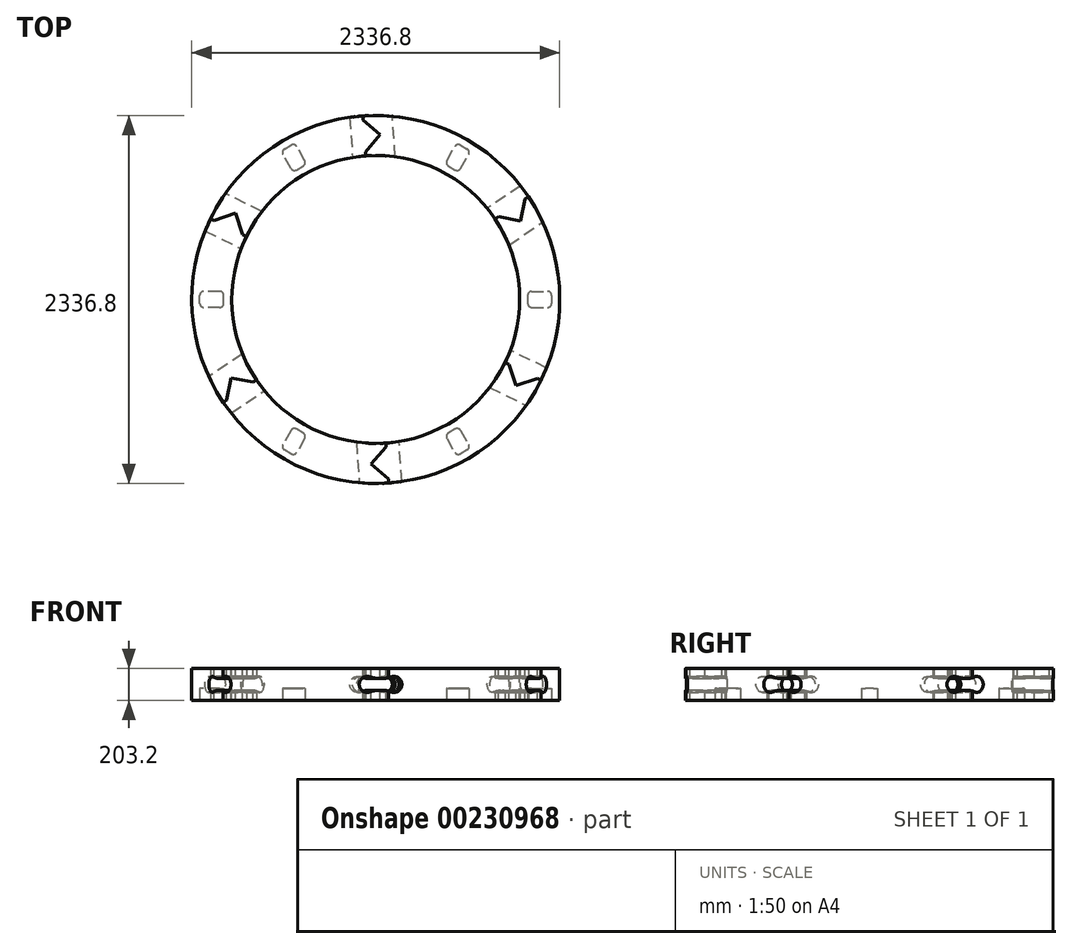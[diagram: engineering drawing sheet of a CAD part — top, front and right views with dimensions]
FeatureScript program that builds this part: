
annotation { "Feature Type Name" : "Feature", "Feature Type Description" : "" }
export const myFeature = defineFeature(function(context is Context, id is Id, definition is map)
    precondition{}
    {
        {
            var Q0;
            Q0=qCreatedBy(makeId("Front.planeOp"),FACE);
            var sketch = newSketch(context, id + "F0", { "sketchPlane" : qUnion([Q0])});
            skLineSegment(sketch, "E0.bottom", {"start": v(-1168.4, 101.6) * mm, "end": v(-914.4, 101.6) * mm});
            skLineSegment(sketch, "E0.top", {"start": v(-1168.4, -101.6) * mm, "end": v(-914.4, -101.6) * mm});
            skLineSegment(sketch, "E0.left", {"start": v(-1168.4, 101.6) * mm, "end": v(-1168.4, -101.6) * mm});
            skLineSegment(sketch, "E0.right", {"start": v(-914.4, 101.6) * mm, "end": v(-914.4, -101.6) * mm});
            skPoint(sketch, "E0.middle", {"position": v(-1041.4, 0) * mm});
            skLineSegment(sketch, "E1", {"start": v(0, 122.44) * mm, "end": v(0, -122.44) * mm, "construction": true});
            skSolve(sketch);
        }
        {
            var Q0;
            Q0=makeQuery(id+"F0.imprint","IMPRINT",FACE,{"disambiguationData":[TD([[makeQuery(id+"F0.imprint","IMPRINT",EDGE,{"derivedFrom":sQuery(id+"F0.wireOp",EDGE,"E0.bottom")}),-1.0]])]});
            var Q1;
            Q1=sQuery(id+"F0.wireOp",EDGE,"E1");
            revolve(context, id + "F1", {"entities" : qUnion([Q0]), "axis" : qUnion([Q1]), "revolveType" : RevolveType.TWO_DIRECTIONS, "angle" : 26 * degree, "angleBack" : 326 * degree});
        }
        {
            var Q0;
            Q0=makeQuery(id+"F1.opRevolve","SWEPT_FACE",FACE,{"disambiguationData":[OSD([sQuery(id+"F0.wireOp",EDGE,"E0.bottom")])]});
            var sketch = newSketch(context, id + "F2", { "sketchPlane" : qUnion([Q0])});
            skLineSegment(sketch, "E2", {"start": v(-1027.32, 501.06) * mm, "end": v(-891.47, 547.84) * mm});
            skLineSegment(sketch, "E3", {"start": v(-891.47, 547.84) * mm, "end": v(-844.69, 411.98) * mm});
            skSolve(sketch);
        }
        {
            var Q0;
            Q0=makeQuery(id+"F2.imprint","IMPRINT",FACE,{"disambiguationData":[TD([[makeQuery(id+"F2.imprint","IMPRINT",EDGE,{"derivedFrom":sQuery(id+"F2.wireOp",EDGE,"E2")}),-1.0]])]});
            var Q1;
            Q1=makeQuery(id+"F1.opRevolve","SWEPT_FACE",FACE,{"disambiguationData":[OSD([sQuery(id+"F0.wireOp",EDGE,"E0.top")])]});
            extrude(context, id + "F3", {"entities" : qUnion([Q0]), "operationType" : NewBodyOperationType.ADD, "endBound" : BoundingType.UP_TO_SURFACE, "oppositeDirection" : true, "endBoundEntityFace" : qUnion([Q1]), "depth" : 25.4 * mm});
        }
        {
            var Q0;
            {var subQ0=sQuery(id+"F0.wireOp",EDGE,"E0.bottom");Q0=makeQuery(id+"F3.boolean.opBoolean","MERGE",FACE,{"derivedFrom":[makeQuery(id+"F1.opRevolve","SWEPT_FACE",FACE,{"disambiguationData":[OSD([subQ0])]}),makeQuery(id+"F3.opExtrude","CAP_FACE",FACE,{"disambiguationData":[OSD([subQ0,sQuery(id+"F2.wireOp",EDGE,"E2"),sQuery(id+"F2.wireOp",EDGE,"E3")])],"isStart":true})]});}
            var sketch = newSketch(context, id + "F4", { "sketchPlane" : qUnion([Q0])});
            skLineSegment(sketch, "E4", {"start": v(-947.59, -639.16) * mm, "end": v(-920.17, -498.11) * mm});
            skLineSegment(sketch, "E5", {"start": v(-920.17, -498.11) * mm, "end": v(-779.13, -525.53) * mm});
            skSolve(sketch);
        }
        {
            var Q0;
            Q0=qSketchRegion(id+"F4",true);
            var Q1;
            Q1=makeQuery(id+"F4.imprint","IMPRINT",FACE,{"disambiguationData":[TD([[makeQuery(id+"F4.imprint","IMPRINT",EDGE,{"derivedFrom":sQuery(id+"F4.wireOp",EDGE,"E4")}),-1.0]])]});
            var Q2;
            {var subQ0=sQuery(id+"F0.wireOp",EDGE,"E0.top");Q2=makeQuery(id+"F3.boolean.opBoolean","MERGE",FACE,{"derivedFrom":[makeQuery(id+"F1.opRevolve","SWEPT_FACE",FACE,{"disambiguationData":[OSD([subQ0])]}),makeQuery(id+"F3.opExtrude","CAP_FACE",FACE,{"disambiguationData":[OSD([subQ0])],"isStart":false})]});}
            extrude(context, id + "F5", {"entities" : qUnion([Q0, Q1]), "operationType" : NewBodyOperationType.REMOVE, "endBound" : BoundingType.UP_TO_SURFACE, "oppositeDirection" : true, "endBoundEntityFace" : qUnion([Q2]), "depth" : 25.4 * mm});
        }
        {
            var Q0;
            Q0=makeQuery(id+"F3.opExtrude","SWEPT_EDGE",EDGE,{"disambiguationData":[OSD([sQuery(id+"F2.wireOp",EDGE,"E2"),sQuery(id+"F2.wireOp",EDGE,"E3")])]});
            var Q1;
            Q1=makeQuery(id+"F3.opExtrude","SWEPT_FACE",FACE,{"disambiguationData":[OSD([sQuery(id+"F2.wireOp",EDGE,"E2")])]});
            cPlane(context, id + "F6", {"entities" : qUnion([Q0, Q1]), "cplaneType" : CPlaneType.LINE_ANGLE, "offset" : 25.4 * mm, "angle" : 45 * degree, "width" : 152.4 * mm, "height" : 152.4 * mm});
        }
        {
            var Q0;
            Q0=makeQuery(id+"F5.boolean.opBoolean","COPY",EDGE,{"derivedFrom":makeQuery(id+"F5.opExtrude","SWEPT_EDGE",EDGE,{"disambiguationData":[OSD([sQuery(id+"F4.wireOp",EDGE,"E4"),sQuery(id+"F4.wireOp",EDGE,"E5")])]})});
            var Q1;
            Q1=makeQuery(id+"F5.boolean.opBoolean","COPY",FACE,{"derivedFrom":makeQuery(id+"F5.opExtrude","SWEPT_FACE",FACE,{"disambiguationData":[OSD([sQuery(id+"F4.wireOp",EDGE,"E4")])]})});
            cPlane(context, id + "F7", {"entities" : qUnion([Q0, Q1]), "cplaneType" : CPlaneType.LINE_ANGLE, "offset" : 25.4 * mm, "angle" : 45 * degree, "width" : 152.4 * mm, "height" : 152.4 * mm});
        }
        {
            var Q0;
            Q0=qCreatedBy(id+"F6.planeOp",FACE);
            var sketch = newSketch(context, id + "F8", { "sketchPlane" : qUnion([Q0])});
            skArc(sketch, "E6", {"start": v(-15.92, 47.62) * mm, "mid": v(-84.4, 0) * mm, "end": v(-15.92, -47.63) * mm});
            skArc(sketch, "E7", {"start": v(117.52, -47.63) * mm, "mid": v(186, 0) * mm, "end": v(117.52, 47.62) * mm});
            skLineSegment(sketch, "E8", {"start": v(37.1, 38.1) * mm, "end": v(64.5, 38.1) * mm});
            skLineSegment(sketch, "E9", {"start": v(37.1, -38.1) * mm, "end": v(64.5, -38.1) * mm});
            skPoint(sketch, "E10.visualSharp", {"position": v(0, 38.1) * mm});
            skArc(sketch, "E10.filletArc", {"start": v(-15.92, 47.63) * mm, "mid": v(10.17, 40.5) * mm, "end": v(37.1, 38.1) * mm});
            skPoint(sketch, "E11.visualSharp", {"position": v(101.6, 38.1) * mm});
            skArc(sketch, "E11.filletArc", {"start": v(64.5, 38.1) * mm, "mid": v(91.43, 40.5) * mm, "end": v(117.52, 47.63) * mm});
            skPoint(sketch, "E12.visualSharp", {"position": v(101.6, -38.1) * mm});
            skArc(sketch, "E12.filletArc", {"start": v(117.52, -47.63) * mm, "mid": v(91.43, -40.5) * mm, "end": v(64.5, -38.1) * mm});
            skPoint(sketch, "E13.visualSharp", {"position": v(0, -38.1) * mm});
            skArc(sketch, "E13.filletArc", {"start": v(37.1, -38.1) * mm, "mid": v(10.17, -40.5) * mm, "end": v(-15.92, -47.63) * mm});
            skSolve(sketch);
        }
        {
            var Q0;
            Q0=qSketchRegion(id+"F8",true);
            extrude(context, id + "F9", {"entities" : qUnion([Q0]), "operationType" : NewBodyOperationType.REMOVE, "endBound" : BoundingType.SYMMETRIC, "oppositeDirection" : true, "depth" : 508 * mm});
        }
        {
            var Q0;
            Q0=qCreatedBy(id+"F7.planeOp",FACE);
            var sketch = newSketch(context, id + "F10", { "sketchPlane" : qUnion([Q0])});
            skArc(sketch, "E14", {"start": v(-117.52, 47.63) * mm, "mid": v(-186, 0) * mm, "end": v(-117.52, -47.63) * mm});
            skArc(sketch, "E15", {"start": v(15.92, -47.63) * mm, "mid": v(84.4, 0) * mm, "end": v(15.92, 47.63) * mm});
            skLineSegment(sketch, "E16", {"start": v(-37.1, 38.1) * mm, "end": v(-64.5, 38.1) * mm});
            skLineSegment(sketch, "E17", {"start": v(-37.1, -38.1) * mm, "end": v(-64.5, -38.1) * mm});
            skPoint(sketch, "E18.visualSharp", {"position": v(0, 38.1) * mm});
            skArc(sketch, "E18.filletArc", {"start": v(-37.1, 38.1) * mm, "mid": v(-10.17, 40.5) * mm, "end": v(15.92, 47.63) * mm});
            skPoint(sketch, "E19.visualSharp", {"position": v(-101.6, 38.1) * mm});
            skArc(sketch, "E19.filletArc", {"start": v(-117.52, 47.62) * mm, "mid": v(-91.43, 40.5) * mm, "end": v(-64.5, 38.1) * mm});
            skPoint(sketch, "E20.visualSharp", {"position": v(-101.6, -38.1) * mm});
            skArc(sketch, "E20.filletArc", {"start": v(-64.5, -38.1) * mm, "mid": v(-91.43, -40.5) * mm, "end": v(-117.52, -47.62) * mm});
            skPoint(sketch, "E21.visualSharp", {"position": v(0, -38.1) * mm});
            skArc(sketch, "E21.filletArc", {"start": v(15.92, -47.63) * mm, "mid": v(-10.17, -40.5) * mm, "end": v(-37.1, -38.1) * mm});
            skSolve(sketch);
        }
        {
            var Q0;
            Q0=qSketchRegion(id+"F10",true);
            extrude(context, id + "F11", {"entities" : qUnion([Q0]), "operationType" : NewBodyOperationType.REMOVE, "endBound" : BoundingType.SYMMETRIC, "oppositeDirection" : true, "depth" : 508 * mm});
        }
        {
            var Q0;
            {var subQ0=sQuery(id+"F0.wireOp",EDGE,"E0.top");Q0=makeQuery(id+"F3.boolean.opBoolean","MERGE",FACE,{"derivedFrom":[makeQuery(id+"F1.opRevolve","SWEPT_FACE",FACE,{"disambiguationData":[OSD([subQ0])]}),makeQuery(id+"F3.opExtrude","CAP_FACE",FACE,{"disambiguationData":[OSD([subQ0])],"isStart":false})]});}
            var sketch = newSketch(context, id + "F12", { "sketchPlane" : qUnion([Q0])});
            skLineSegment(sketch, "E22.bottom", {"start": v(-990.6, 50.8) * mm, "end": v(-1092.2, 50.8) * mm});
            skLineSegment(sketch, "E22.top", {"start": v(-990.6, -50.8) * mm, "end": v(-1092.2, -50.8) * mm});
            skLineSegment(sketch, "E22.left", {"start": v(-965.2, 25.4) * mm, "end": v(-965.2, -25.4) * mm});
            skLineSegment(sketch, "E22.right", {"start": v(-1117.6, 25.4) * mm, "end": v(-1117.6, -25.4) * mm});
            skPoint(sketch, "E22.middle", {"position": v(-1041.4, 0) * mm});
            skPoint(sketch, "E23.visualSharp", {"position": v(-965.2, 50.8) * mm});
            skArc(sketch, "E23.filletArc", {"start": v(-965.2, 25.4) * mm, "mid": v(-972.64, 43.36) * mm, "end": v(-990.6, 50.8) * mm});
            skPoint(sketch, "E24.visualSharp", {"position": v(-965.2, -50.8) * mm});
            skArc(sketch, "E24.filletArc", {"start": v(-990.6, -50.8) * mm, "mid": v(-972.64, -43.36) * mm, "end": v(-965.2, -25.4) * mm});
            skPoint(sketch, "E25.visualSharp", {"position": v(-1117.6, -50.8) * mm});
            skArc(sketch, "E25.filletArc", {"start": v(-1117.6, -25.4) * mm, "mid": v(-1110.16, -43.36) * mm, "end": v(-1092.2, -50.8) * mm});
            skPoint(sketch, "E26.visualSharp", {"position": v(-1117.6, 50.8) * mm});
            skArc(sketch, "E26.filletArc", {"start": v(-1092.2, 50.8) * mm, "mid": v(-1110.16, 43.36) * mm, "end": v(-1117.6, 25.4) * mm});
            skSolve(sketch);
        }
        {
            var Q0;
            Q0=qSketchRegion(id+"F12",true);
            extrude(context, id + "F13", {"entities" : qUnion([Q0]), "operationType" : NewBodyOperationType.REMOVE, "oppositeDirection" : true, "depth" : 76.2 * mm});
        }
        {
            var Q0;
            Q0=makeQuery(id+"F1.opRevolve","SWEPT_BODY",BODY,{"disambiguationData":[OSD([sQuery(id+"F0.wireOp",EDGE,"E0.bottom"),sQuery(id+"F0.wireOp",EDGE,"E0.top"),sQuery(id+"F0.wireOp",EDGE,"E0.left"),sQuery(id+"F0.wireOp",EDGE,"E0.right")])]});
            var Q1;
            Q1=sQuery(id+"F0.wireOp",EDGE,"E1");
            circularPattern(context, id + "F14", {"entities" : qUnion([Q0]), "axis" : qUnion([Q1]), "angle" : 360 * degree, "instanceCount" : 6, "equalSpace" : true});
        }
    });
